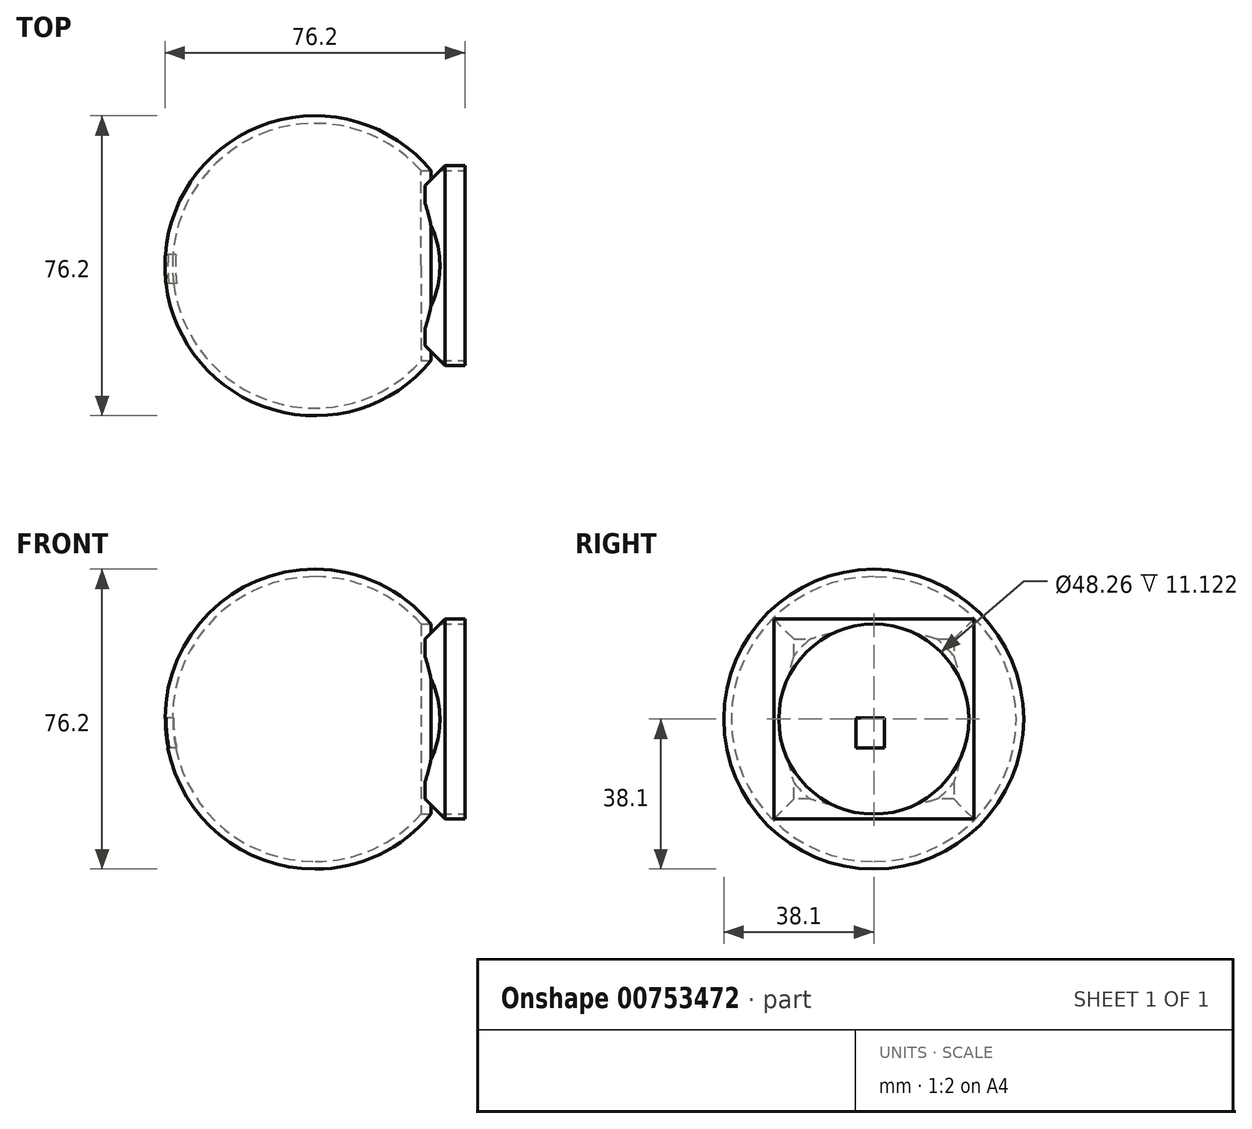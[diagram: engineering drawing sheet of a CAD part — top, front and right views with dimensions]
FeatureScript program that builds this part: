
annotation { "Feature Type Name" : "Feature", "Feature Type Description" : "" }
export const myFeature = defineFeature(function(context is Context, id is Id, definition is map)
    precondition{}
    {
        {
            var Q0;
            Q0=qCreatedBy(makeId("Front.planeOp"),FACE);
            var sketch = newSketch(context, id + "F0", { "sketchPlane" : qUnion([Q0])});
            skLineSegment(sketch, "E0", {"start": v(0, 0) * mm, "end": v(0, 76.2) * mm});
            skArc(sketch, "E1", {"start": v(0, 0) * mm, "mid": v(38.1, 38.1) * mm, "end": v(0, 76.2) * mm});
            skPoint(sketch, "E2", {"position": v(38.1, 38.1) * mm});
            skPoint(sketch, "E3", {"position": v(0, 0) * mm});
            skPoint(sketch, "E4", {"position": v(0, 1.9) * mm});
            skPoint(sketch, "E5", {"position": v(0, 74.3) * mm});
            skArc(sketch, "E6", {"start": v(0, 1.9) * mm, "mid": v(36.2, 38.1) * mm, "end": v(0, 74.3) * mm});
            skSolve(sketch);
        }
        {
            var Q0;
            Q0=makeQuery(id+"F0.imprint","IMPRINT",FACE,{"disambiguationData":[TD([[makeQuery(id+"F0.imprint","IMPRINT",EDGE,{"derivedFrom":sQuery(id+"F0.wireOp",EDGE,"E0")}),-1.0]])]});
            var Q1;
            Q1=sQuery(id+"F0.wireOp",EDGE,"E0");
            revolve(context, id + "F1", {"surfaceOperationType" : NewSurfaceOperationType.NEW, "entities" : qUnion([Q0]), "axis" : qUnion([Q1]), "revolveType" : RevolveType.FULL});
        }
        {
            var Q0;
            Q0=qCreatedBy(makeId("Right.planeOp"),FACE);
            cPlane(context, id + "F2", {"entities" : qUnion([Q0]), "cplaneType" : CPlaneType.OFFSET, "offset" : 38.1 * mm, "width" : 152.4 * mm, "height" : 152.4 * mm});
        }
        {
            var Q0;
            Q0=qCreatedBy(id+"F2.planeOp",FACE);
            var sketch = newSketch(context, id + "F3", { "sketchPlane" : qUnion([Q0])});
            skLineSegment(sketch, "E7.bottom", {"start": v(-25.4, 12.7) * mm, "end": v(25.4, 12.7) * mm});
            skLineSegment(sketch, "E7.top", {"start": v(-25.4, 63.5) * mm, "end": v(25.4, 63.5) * mm});
            skLineSegment(sketch, "E7.left", {"start": v(-25.4, 12.7) * mm, "end": v(-25.4, 63.5) * mm});
            skLineSegment(sketch, "E7.right", {"start": v(25.4, 12.7) * mm, "end": v(25.4, 63.5) * mm});
            skPoint(sketch, "E8", {"position": v(0, 64.06) * mm});
            skPoint(sketch, "E9", {"position": v(0, 31.75) * mm});
            skPoint(sketch, "E10", {"position": v(25.4, 31.75) * mm});
            skSolve(sketch);
        }
        {
            var Q0;
            Q0 = qSketchRegion(id + "F3", true);
            extrude(context, id + "F4", {"entities" : qUnion([Q0]), "operationType" : NewBodyOperationType.ADD, "oppositeDirection" : true, "depth" : 10.16 * mm, "offsetDistance" : 25.4 * mm});
        }
        {
            var Q0;
            {var subQ0=sQuery(id+"F3.wireOp",EDGE,"E7.bottom");var subQ1=sQuery(id+"F3.wireOp",EDGE,"E7.right");Q0=makeQuery(id+"F4.boolean.opBoolean","SPLIT",EDGE,{"disambiguationData":[TD([makeQuery(id+"F4.opExtrude","SWEPT_FACE",FACE,{"disambiguationData":[OSD([subQ0])]})])],"derivedFrom":makeQuery(id+"F4.opExtrude","CAP_EDGE",EDGE,{"disambiguationData":[OSD([subQ1])],"isStart":false})});}
            var Q1;
            {var subQ0=sQuery(id+"F3.wireOp",EDGE,"E7.right");var subQ1=sQuery(id+"F3.wireOp",EDGE,"E7.top");Q1=makeQuery(id+"F4.boolean.opBoolean","SPLIT",EDGE,{"disambiguationData":[TD([makeQuery(id+"F4.opExtrude","SWEPT_FACE",FACE,{"disambiguationData":[OSD([subQ1])]})])],"derivedFrom":makeQuery(id+"F4.opExtrude","CAP_EDGE",EDGE,{"disambiguationData":[OSD([subQ0])],"isStart":false})});}
            var Q2;
            {var subQ0=sQuery(id+"F3.wireOp",EDGE,"E7.bottom");var subQ1=sQuery(id+"F3.wireOp",EDGE,"E7.left");Q2=makeQuery(id+"F4.boolean.opBoolean","SPLIT",EDGE,{"disambiguationData":[TD([makeQuery(id+"F4.opExtrude","SWEPT_FACE",FACE,{"disambiguationData":[OSD([subQ1])]})])],"derivedFrom":makeQuery(id+"F4.opExtrude","CAP_EDGE",EDGE,{"disambiguationData":[OSD([subQ0])],"isStart":false})});}
            var Q3;
            {var subQ0=sQuery(id+"F3.wireOp",EDGE,"E7.bottom");var subQ1=sQuery(id+"F3.wireOp",EDGE,"E7.right");Q3=makeQuery(id+"F4.boolean.opBoolean","SPLIT",EDGE,{"disambiguationData":[TD([makeQuery(id+"F4.opExtrude","SWEPT_FACE",FACE,{"disambiguationData":[OSD([subQ1])]})])],"derivedFrom":makeQuery(id+"F4.opExtrude","CAP_EDGE",EDGE,{"disambiguationData":[OSD([subQ0])],"isStart":false})});}
            var Q4;
            {var subQ0=sQuery(id+"F3.wireOp",EDGE,"E7.bottom");var subQ1=sQuery(id+"F3.wireOp",EDGE,"E7.left");Q4=makeQuery(id+"F4.boolean.opBoolean","SPLIT",EDGE,{"disambiguationData":[TD([makeQuery(id+"F4.opExtrude","SWEPT_FACE",FACE,{"disambiguationData":[OSD([subQ0])]})])],"derivedFrom":makeQuery(id+"F4.opExtrude","CAP_EDGE",EDGE,{"disambiguationData":[OSD([subQ1])],"isStart":false})});}
            var Q5;
            {var subQ0=sQuery(id+"F3.wireOp",EDGE,"E7.left");var subQ1=sQuery(id+"F3.wireOp",EDGE,"E7.top");Q5=makeQuery(id+"F4.boolean.opBoolean","SPLIT",EDGE,{"disambiguationData":[TD([makeQuery(id+"F4.opExtrude","SWEPT_FACE",FACE,{"disambiguationData":[OSD([subQ0])]})])],"derivedFrom":makeQuery(id+"F4.opExtrude","CAP_EDGE",EDGE,{"disambiguationData":[OSD([subQ1])],"isStart":false})});}
            var Q6;
            {var subQ0=sQuery(id+"F3.wireOp",EDGE,"E7.right");var subQ1=sQuery(id+"F3.wireOp",EDGE,"E7.top");Q6=makeQuery(id+"F4.boolean.opBoolean","SPLIT",EDGE,{"disambiguationData":[TD([makeQuery(id+"F4.opExtrude","SWEPT_FACE",FACE,{"disambiguationData":[OSD([subQ0])]})])],"derivedFrom":makeQuery(id+"F4.opExtrude","CAP_EDGE",EDGE,{"disambiguationData":[OSD([subQ1])],"isStart":false})});}
            var Q7;
            {var subQ0=sQuery(id+"F3.wireOp",EDGE,"E7.left");var subQ1=sQuery(id+"F3.wireOp",EDGE,"E7.top");Q7=makeQuery(id+"F4.boolean.opBoolean","SPLIT",EDGE,{"disambiguationData":[TD([makeQuery(id+"F4.opExtrude","SWEPT_FACE",FACE,{"disambiguationData":[OSD([subQ1])]})])],"derivedFrom":makeQuery(id+"F4.opExtrude","CAP_EDGE",EDGE,{"disambiguationData":[OSD([subQ0])],"isStart":false})});}
            chamfer(context, id + "F5", {"entities" : qUnion([Q0, Q1, Q2, Q3, Q4, Q5, Q6, Q7]), "width" : 5.08 * mm, "tangentPropagation" : true});
        }
        {
            var Q0;
            Q0=makeQuery(id+"F4.opExtrude","CAP_FACE",FACE,{"disambiguationData":[OSD([sQuery(id+"F3.wireOp",EDGE,"E7.bottom"),sQuery(id+"F3.wireOp",EDGE,"E7.top"),sQuery(id+"F3.wireOp",EDGE,"E7.left"),sQuery(id+"F3.wireOp",EDGE,"E7.right")])],"isStart":true});
            var sketch = newSketch(context, id + "F6", { "sketchPlane" : qUnion([Q0])});
            skPoint(sketch, "E11", {"position": v(0, 38.1) * mm});
            skCircle(sketch, "E12", {"center": v(0, 38.1) * mm, "radius": 24.13 * mm});
            skSolve(sketch);
        }
        {
            var Q0;
            Q0=makeQuery(id+"F6.imprint","IMPRINT",FACE,{"disambiguationData":[TD([[makeQuery(id+"F6.imprint","IMPRINT",EDGE,{"derivedFrom":sQuery(id+"F6.wireOp",EDGE,"E12")}),1.0]])]});
            extrude(context, id + "F7", {"entities" : qUnion([Q0]), "operationType" : NewBodyOperationType.REMOVE, "oppositeDirection" : true, "depth" : 25.4 * mm, "offsetDistance" : 25.4 * mm});
        }
        {
            var Q0;
            Q0=qCreatedBy(makeId("Right.planeOp"),FACE);
            cPlane(context, id + "F8", {"entities" : qUnion([Q0]), "cplaneType" : CPlaneType.OFFSET, "offset" : 38.1 * mm, "oppositeDirection" : true, "width" : 152.4 * mm, "height" : 152.4 * mm});
        }
        {
            var Q0;
            Q0=qCreatedBy(id+"F8.planeOp",FACE);
            var sketch = newSketch(context, id + "F9", { "sketchPlane" : qUnion([Q0])});
            skLineSegment(sketch, "E13.bottom", {"start": v(2.78, 38.36) * mm, "end": v(-4.5, 38.36) * mm});
            skLineSegment(sketch, "E13.top", {"start": v(2.78, 30.74) * mm, "end": v(-4.5, 30.74) * mm});
            skLineSegment(sketch, "E13.left", {"start": v(2.78, 38.36) * mm, "end": v(2.78, 30.74) * mm});
            skLineSegment(sketch, "E13.right", {"start": v(-4.5, 38.36) * mm, "end": v(-4.5, 30.74) * mm});
            skSolve(sketch);
        }
        {
            var Q0;
            Q0=makeQuery(id+"F9.imprint","IMPRINT",FACE,{"disambiguationData":[TD([[makeQuery(id+"F9.imprint","IMPRINT",EDGE,{"derivedFrom":sQuery(id+"F9.wireOp",EDGE,"E13.bottom")}),1.0]])]});
            extrude(context, id + "F10", {"entities" : qUnion([Q0]), "operationType" : NewBodyOperationType.REMOVE, "endBound" : BoundingType.THROUGH_ALL, "depth" : 25.4 * mm, "offsetDistance" : 25.4 * mm});
        }
    });
